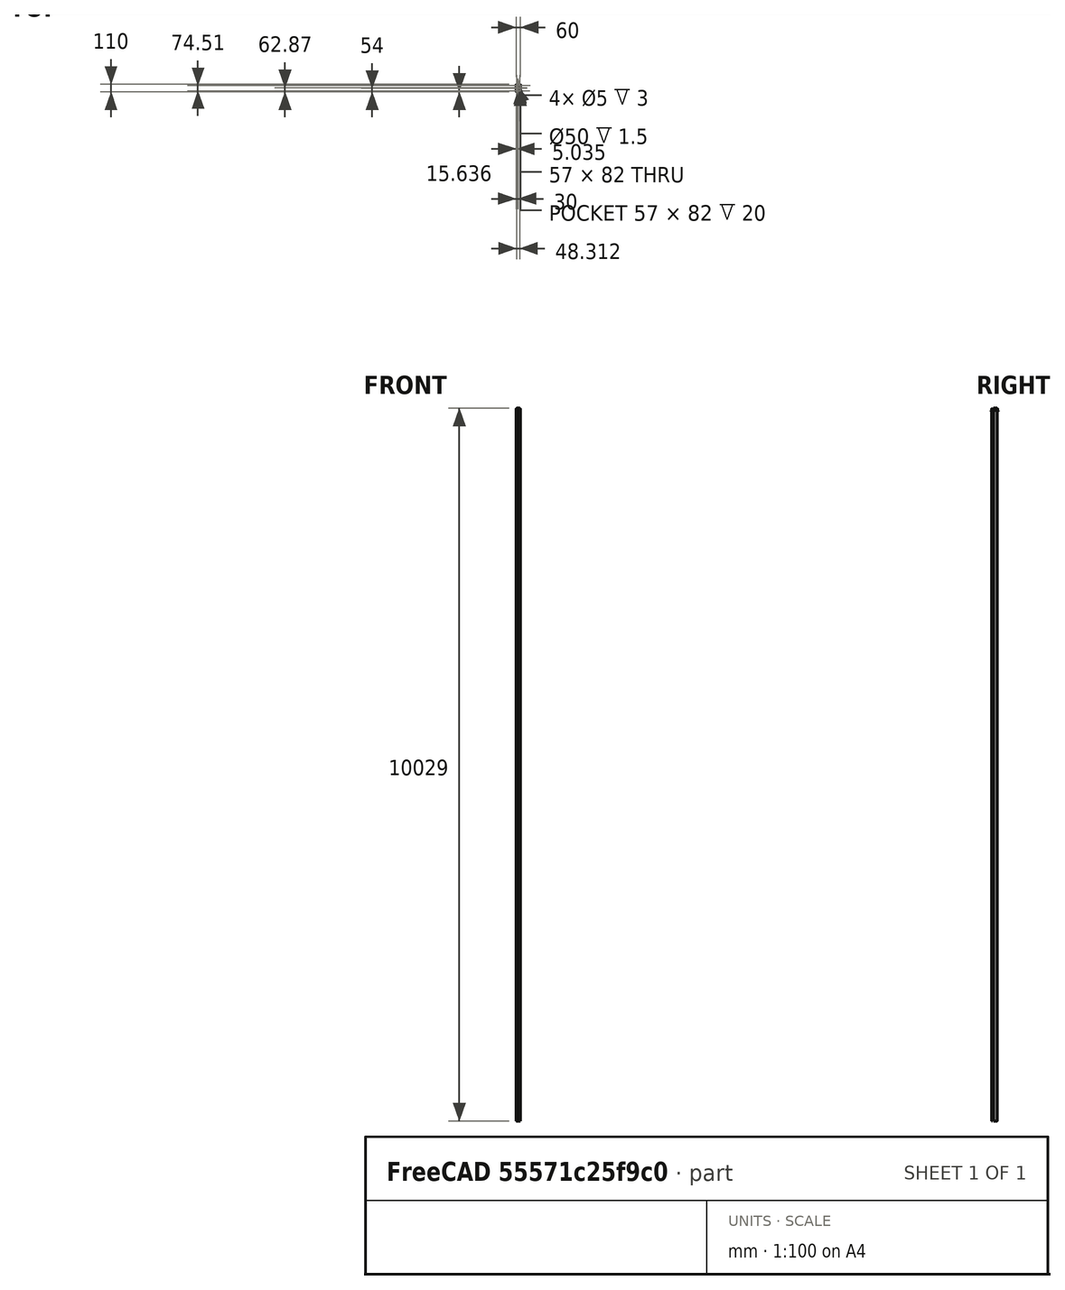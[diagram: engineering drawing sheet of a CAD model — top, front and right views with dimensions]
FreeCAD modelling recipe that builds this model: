
FCSTD DOCUMENT  (FreeCAD 0.16R4740 (Git))
Label: NotifierEnclosurev2
License: CC-BY 3.0
LicenseURL: http://creativecommons.org/licenses/by/3.0/
objects: Sketcher::SketchObject×11, Part::Box×6, Part::FeaturePython×6, PartDesign::Pad×5, Part::MultiFuse×5, Part::Cut×5, PartDesign::Pocket×4, App::DocumentObjectGroup×2, Part::Thickness×2, Part::Part2DObjectPython×2, PartDesign::Fillet×2, Part::Offset×2, Part::Sweep×2, Part::Cylinder×1, Part::Fillet×1
note: 63 computed .brp shape members not serialized (recipe doc carries the construction recipe); baked Part::Feature solids carry a one-line shape summary decoded from their .brp

FEATURE [Part::Box] Box  label="Cube"
  Height = 20
  Length = 57
  Width = 82
FEATURE [Part::Box] Box001  label="Base"
  Height = 1.6
  Length = 54
  Placement = pos=(0,0,3) rot=(0,0,1;0rad)
  Width = 80
FEATURE [Part::Box] Box002  label="EthernetJack"
  Height = 13.6
  Length = 16
  Placement = pos=(11.2,-4.6,4.6) rot=(0,0,1;0rad)
  Width = 21
FEATURE [Part::Box] Box003  label="PowerJack"
  Height = 11
  Length = 9
  Placement = pos=(43.4,-4.5,4.6) rot=(0,0,1;0rad)
  Width = 14.5
FEATURE [Sketcher::SketchObject] Sketch
  ExternalGeometry = -> [Box001]
  Placement = pos=(0,0,4.6) rot=(0,0,1;0rad)
  Support = -> Box001 [Face6]
  sketch-geometry (6):
    g0: Circle CenterX=2.2 CenterY=77.12 CenterZ=0 NormalX=0 NormalY=0 NormalZ=1 Radius=1.5
    g1: Circle CenterX=50.25 CenterY=76.75 CenterZ=0 NormalX=0 NormalY=0 NormalZ=1 Radius=1.5
    g2: Circle CenterX=2 CenterY=2.7 CenterZ=0 NormalX=0 NormalY=0 NormalZ=1 Radius=1.5
    g3: Circle CenterX=39.8 CenterY=2.7 CenterZ=0 NormalX=0 NormalY=0 NormalZ=1 Radius=1.5
    g4: LineSegment [constr] StartX=0.5 StartY=1.2 StartZ=0 EndX=0.5 EndY=5.19188 EndZ=0
    g5: LineSegment [constr] StartX=0.5 StartY=1.2 StartZ=0 EndX=4.53205 EndY=1.2 EndZ=0
  constraints (17):
    c: Radius(g2) = 1.5
    c: Vertical(g4)
    c: Tangent(g4,g2)
    c: Horizontal(g5)
    c: Tangent(g5,g2)
    c: Coincident(g4,g5)
    c: DistanceX(g-1,g4) = 0.5
    c: DistanceY(g-1,g5) = 1.2
    c: Equal(g3,g2)
    c: DistanceY(g-1,g3) = 2.7
    c: DistanceX(g3,g-3) = 14.2
    c: Equal(g0,g1)
    c: Equal(g1,g2)
    c: DistanceY(g0,g-4) = 2.88
    c: DistanceX(g0,g-4) = -2.2
    c: DistanceX(g1,g-4) = 3.75
    c: DistanceY(g1,g-4) = 3.25
FEATURE [PartDesign::Pocket] Pocket  label="Holes"
  Length = 5
  Placement = pos=(0,0,3) rot=(0,0,1;0rad)
  Sketch = -> Sketch
  Type = 1
FEATURE [App::DocumentObjectGroup] Group  label="iBoard"
  Group = -> [Box001,Box002,Box003,Pocket]
FEATURE [Part::Thickness] Thickness
  Faces = -> Box [Face6]
  Intersection = false
  Join = 0
  Mode = 0
  Placement = pos=(-1.5,0,0) rot=(0,0,1;0rad)
  SelfIntersection = false
  Value = 1.5
FEATURE [Sketcher::SketchObject] Sketch001
  ExternalGeometry = -> [Thickness]
  Placement = pos=(-1.5,0,20) rot=(0,0,1;0rad)
  Support = -> Thickness [Face6]
  sketch-geometry (8):
    g0: LineSegment StartX=-1.5 StartY=0 StartZ=0 EndX=-1.5 EndY=82 EndZ=0
    g1: LineSegment StartX=0 StartY=83.5 StartZ=0 EndX=57 EndY=83.5 EndZ=0
    g2: LineSegment StartX=58.5 StartY=0 StartZ=0 EndX=58.5 EndY=82 EndZ=0
    g3: LineSegment StartX=0 StartY=-1.5 StartZ=0 EndX=57 EndY=-1.5 EndZ=0
    g4: ArcOfCircle CenterX=0 CenterY=0 CenterZ=0 NormalX=0 NormalY=0 NormalZ=1 Radius=1.5 StartAngle=3.14159 EndAngle=4.71239
    g5: ArcOfCircle CenterX=0 CenterY=82 CenterZ=0 NormalX=0 NormalY=0 NormalZ=1 Radius=1.5 StartAngle=1.5708 EndAngle=3.14159
    g6: ArcOfCircle CenterX=57 CenterY=82 CenterZ=0 NormalX=0 NormalY=0 NormalZ=1 Radius=1.5 StartAngle=0 EndAngle=1.5708
    g7: ArcOfCircle CenterX=57 CenterY=0 CenterZ=0 NormalX=0 NormalY=0 NormalZ=1 Radius=1.5 StartAngle=4.71239 EndAngle=6.28319
  constraints (24):
    c: Vertical(g0)
    c: Horizontal(g1)
    c: Vertical(g2)
    c: Horizontal(g3)
    c: Coincident(g0,g-10)
    c: Coincident(g0,g-4)
    c: Coincident(g-10,g3)
    c: Coincident(g3,g-9)
    c: Coincident(g2,g-8)
    c: Coincident(g2,g-7)
    c: Coincident(g1,g-6)
    c: Coincident(g1,g-5)
    c: Coincident(g4,g-1)
    c: Coincident(g4,g3)
    c: Coincident(g4,g0)
    c: Coincident(g5,g-3)
    c: Coincident(g5,g0)
    c: Coincident(g5,g1)
    c: Coincident(g6,g-6)
    c: Coincident(g6,g1)
    c: Coincident(g6,g2)
    c: Coincident(g7,g-8)
    c: Coincident(g7,g2)
    c: Coincident(g7,g3)
FEATURE [Part::Part2DObjectPython] Clone2D  label="Clone of Sketch001 (2D)"  # Draft 2D object (typed FeaturePython)
  Objects = -> [Sketch001]
  Placement = pos=(-1.5,0,20) rot=(0,0,1;0rad)
  Scale = (1,1,1)
FEATURE [PartDesign::Pad] Pad
  Length = 1.5
  Length2 = 100
  Placement = pos=(-1.5,0,20) rot=(0,0,1;0rad)
  Sketch = -> Clone2D
  Type = 0
FEATURE [PartDesign::Fillet] Fillet
  Base = -> Pad [Edge22,Edge24,Edge19,Edge13,Edge7,Edge4,Edge16,Edge10]
  Placement = pos=(-1.5,0,20) rot=(0,0,1;0rad)
  Radius = 0.5
FEATURE [Sketcher::SketchObject] Sketch002
  ExternalGeometry = -> [Fillet]
  Placement = pos=(-1.5,0,21.5) rot=(0,0,1;0rad)
  Support = -> Fillet [Face8]
  sketch-geometry (2):
    g0: Circle CenterX=28.5 CenterY=49.8696 CenterZ=0 NormalX=0 NormalY=0 NormalZ=1 Radius=25
    g1: LineSegment [constr] StartX=28.5 StartY=49.8696 StartZ=0 EndX=28.5 EndY=88.1673 EndZ=0
  constraints (4):
    c: Radius(g0) = 25
    c: Coincident(g1,g0)
    c: Vertical(g1)
    c: Symmetric(g-5,g-3,g1)
FEATURE [PartDesign::Pocket] Pocket001
  Length = 5
  Placement = pos=(-1.5,0,20) rot=(0,0,1;0rad)
  Sketch = -> Sketch002
  Type = 1
FEATURE [Sketcher::SketchObject] Sketch003
  Placement = pos=(-1.5,0,0) rot=(0,0,1;0rad)
  Support = -> Thickness [Face5]
  sketch-geometry (4):
    g0: Circle CenterX=3.53528 CenterY=2.63614 CenterZ=0 NormalX=0 NormalY=0 NormalZ=1 Radius=2.5
    g1: Circle CenterX=41.3722 CenterY=2.74074 CenterZ=0 NormalX=0 NormalY=0 NormalZ=1 Radius=2.5
    g2: Circle CenterX=3.78181 CenterY=77.146 CenterZ=0 NormalX=0 NormalY=0 NormalZ=1 Radius=2.5
    g3: Circle CenterX=51.8469 CenterY=76.7239 CenterZ=0 NormalX=0 NormalY=0 NormalZ=1 Radius=2.5
  constraints (4):
    c: Radius(g0) = 2.5
    c: Equal(g0,g1)
    c: Equal(g1,g2)
    c: Equal(g2,g3)
FEATURE [PartDesign::Pad] Pad001
  Length = 3
  Length2 = 100
  Placement = pos=(-1.5,0,0) rot=(0,0,1;0rad)
  Sketch = -> Sketch003
  Type = 0
FEATURE [Sketcher::SketchObject] Sketch004
  ExternalGeometry = -> [Pad001]
  Placement = pos=(-1.5,0,3) rot=(0,0,1;0rad)
  Support = -> Pad001 [Face30]
  sketch-geometry (4):
    g0: Circle CenterX=3.78181 CenterY=77.146 CenterZ=0 NormalX=0 NormalY=0 NormalZ=1 Radius=1.4
    g1: Circle CenterX=51.8469 CenterY=76.7239 CenterZ=0 NormalX=0 NormalY=0 NormalZ=1 Radius=1.4
    g2: Circle CenterX=3.53528 CenterY=2.63614 CenterZ=0 NormalX=0 NormalY=0 NormalZ=1 Radius=1.4
    g3: Circle CenterX=41.3722 CenterY=2.74074 CenterZ=0 NormalX=0 NormalY=0 NormalZ=1 Radius=1.4
  constraints (8):
    c: Coincident(g0,g-3)
    c: Coincident(g1,g-4)
    c: Coincident(g2,g-5)
    c: Coincident(g3,g-6)
    c: Radius(g1) = 1.4
    c: Equal(g1,g0)
    c: Equal(g0,g2)
    c: Equal(g2,g3)
FEATURE [PartDesign::Pocket] Pocket002
  Length = 3
  Placement = pos=(-1.5,0,0) rot=(0,0,1;0rad)
  Sketch = -> Sketch004
  Type = 0
FEATURE [Sketcher::SketchObject] Sketch005
  ExternalGeometry = -> [Pocket001]
  Placement = pos=(-1.5,0,20) rot=(1,0,0;3.14159rad)
  Support = -> Pocket001 [Face4]
  sketch-geometry (8):
    g0: LineSegment StartX=0.2 StartY=-0.2 StartZ=0 EndX=56.8 EndY=-0.2 EndZ=0
    g1: LineSegment StartX=56.8 StartY=-0.2 StartZ=0 EndX=56.8 EndY=-81.8 EndZ=0
    g2: LineSegment StartX=56.8 StartY=-81.8 StartZ=0 EndX=0.2 EndY=-81.8 EndZ=0
    g3: LineSegment StartX=0.2 StartY=-81.8 StartZ=0 EndX=0.2 EndY=-0.2 EndZ=0
    g4: LineSegment StartX=1.5 StartY=-1.5 StartZ=0 EndX=55.5 EndY=-1.5 EndZ=0
    g5: LineSegment StartX=55.5 StartY=-1.5 StartZ=0 EndX=55.5 EndY=-80.5 EndZ=0
    g6: LineSegment StartX=55.5 StartY=-80.5 StartZ=0 EndX=1.5 EndY=-80.5 EndZ=0
    g7: LineSegment StartX=1.5 StartY=-80.5 StartZ=0 EndX=1.5 EndY=-1.5 EndZ=0
  constraints (12):
    c: DistanceX(g-1,g3) = 0.2
    c: DistanceY(g-1,g0) = -0.2
    c: Coincident(g0,g3)
    c: DistanceY(g0,g-3) = 0.2
    c: DistanceX(g1,g-3) = 0.2
    c: Coincident(g1,g0)
    c: DistanceX(g1,g-6) = 0.2
    c: DistanceY(g2,g-6) = -0.2
    c: Coincident(g2,g1)
    c: DistanceX(g3,g-5) = -0.2
    c: DistanceY(g2,g-5) = -0.2
    c: Coincident(g2,g3)
FEATURE [PartDesign::Pad] Pad002
  Length = 2
  Length2 = 100
  Placement = pos=(-1.5,0,20) rot=(0,0,1;0rad)
  Sketch = -> Sketch005
  Type = 0
FEATURE [App::DocumentObjectGroup] Group001  label="Lid"
  Group = -> [Pad,Fillet,Pocket001,Pad002]
FEATURE [Part::Box] Box004  label="Tab1"
  Height = 10
  Length = 8
  Placement = pos=(0,0.2,8) rot=(0,0,1;0rad)
  Width = 1.5
FEATURE [Part::FeaturePython] Clone  label="Clone of Tab1"  # Draft clone (typed FeaturePython)
  Objects = -> [Box004]
  Placement = pos=(32,0.2,8) rot=(0,0,1;0rad)
  Scale = (1,1,1)
FEATURE [Part::FeaturePython] Clone001  label="Clone of Tab002"  # Draft clone (typed FeaturePython)
  Objects = -> [Box004]
  Placement = pos=(0,80.3,8) rot=(0,0,1;0rad)
  Scale = (1,1,1)
FEATURE [Part::FeaturePython] Clone002  label="Clone of Tab003"  # Draft clone (typed FeaturePython)
  Objects = -> [Box004]
  Placement = pos=(46,80.3,8) rot=(0,0,1;0rad)
  Scale = (1,1,1)
FEATURE [Part::Cylinder] Cylinder
  Angle = 360
  Height = 10
  Placement = pos=(4,6,14) rot=(1,0,0;1.5708rad)
  Radius = 1.4
FEATURE [Part::MultiFuse] Fusion  label="LidFusion"
  Shapes = -> [Pad002,Box004,Clone,Clone001,Clone002]
FEATURE [Part::FeaturePython] Clone003  label="Clone of Cylinder"  # Draft clone (typed FeaturePython)
  Objects = -> [Cylinder]
  Placement = pos=(36,6,14) rot=(1,0,0;1.5708rad)
  Scale = (1,1,1)
FEATURE [Part::FeaturePython] Clone004  label="Clone of Cylinder001"  # Draft clone (typed FeaturePython)
  Objects = -> [Cylinder]
  Placement = pos=(4,86,14) rot=(1,0,0;1.5708rad)
  Scale = (1,1,1)
FEATURE [Part::FeaturePython] Clone005  label="Clone of Cylinder002"  # Draft clone (typed FeaturePython)
  Objects = -> [Cylinder]
  Placement = pos=(50,86,14) rot=(1,0,0;1.5708rad)
  Scale = (1,1,1)
FEATURE [Part::MultiFuse] Fusion001
  Shapes = -> [Clone005,Clone004,Clone003,Cylinder]
FEATURE [Part::Cut] Cut
  Base = -> Fusion
  Tool = -> Fusion001
FEATURE [Part::Cut] Cut001
  Base = -> Pocket002
  Tool = -> Fusion001
FEATURE [Part::Offset] Offset
  Fill = false
  Intersection = false
  Join = 2
  Mode = 0
  SelfIntersection = false
  Source = -> Box002
  Value = 1
FEATURE [Part::Offset] Offset001
  Fill = false
  Intersection = false
  Join = 2
  Mode = 0
  SelfIntersection = false
  Source = -> Box003
  Value = 1
FEATURE [Part::MultiFuse] Fusion002
  Shapes = -> [Offset,Offset001]
FEATURE [Part::Cut] Cut002
  Base = -> Cut001
  Tool = -> Fusion002
FEATURE [Part::Cut] Cut003  label="Lid001"
  Base = -> Cut
  Tool = -> Offset
FEATURE [Sketcher::SketchObject] Sketch006
  ExternalGeometry = -> [Cut003]
  Placement = pos=(0,0,21.5) rot=(0,0,1;0rad)
  Support = -> Cut003 [Face60]
  sketch-geometry (1):
    g0: Circle CenterX=27 CenterY=49.8696 CenterZ=0 NormalX=0 NormalY=0 NormalZ=1 Radius=24.5
  constraints (2):
    c: Coincident(g0,g-3)
    c: Radius(g0) = 24.5
FEATURE [Part::Part2DObjectPython] Clone2D001  label="Clone of Sketch006 (2D)"  # Draft 2D object (typed FeaturePython)
  Objects = -> [Sketch006]
  Placement = pos=(0,0,20.5) rot=(0,0,1;0rad)
  Scale = (1,1,1)
FEATURE [PartDesign::Pad] Pad003
  Length = 10
  Length2 = 100
  Placement = pos=(0,0,20.5) rot=(0,0,1;0rad)
  Sketch = -> Clone2D001
  Type = 0
FEATURE [PartDesign::Fillet] Fillet001
  Base = -> Pad003 [Edge3]
  Placement = pos=(0,0,20.5) rot=(0,0,1;0rad)
  Radius = 5
FEATURE [Sketcher::SketchObject] Sketch007
  ExternalGeometry = -> [Fillet001]
  Placement = pos=(0,0,20.5) rot=(1,0,0;3.14159rad)
  Support = -> Fillet001 [Face3]
  sketch-geometry (1):
    g0: Circle CenterX=27 CenterY=-49.8696 CenterZ=0 NormalX=0 NormalY=0 NormalZ=1 Radius=26.5
  constraints (2):
    c: Coincident(g0,g-3)
    c: Radius(g0) = 26.5
FEATURE [PartDesign::Pad] Pad004
  Length = 1.5
  Length2 = 100
  Placement = pos=(0,0,20.5) rot=(0,0,1;0rad)
  Sketch = -> Sketch007
  Type = 0
FEATURE [Part::Thickness] Thickness001
  Faces = -> Pad004 [Face3]
  Intersection = false
  Join = 0
  Mode = 0
  SelfIntersection = false
  Value = -1.5
FEATURE [Part::Box] Box005  label="Cube001"
  Height = 1.5
  Length = 58
  Placement = pos=(-2,-13,-1.5) rot=(0,0,1;0rad)
  Width = 110
FEATURE [Part::Fillet] Fillet002
  Base = -> Box005
  Edges = 4 edges r=5: [Edge1,Edge3,Edge5,Edge7]
FEATURE [Sketcher::SketchObject] Sketch008
  ExternalGeometry = -> [Fillet002]
  Support = -> Fillet002 [Face2]
  sketch-geometry (4):
    g0: Circle CenterX=3 CenterY=92 CenterZ=0 NormalX=0 NormalY=0 NormalZ=1 Radius=1.5
    g1: Circle CenterX=51 CenterY=92 CenterZ=0 NormalX=0 NormalY=0 NormalZ=1 Radius=1.5
    g2: Circle CenterX=3 CenterY=-8 CenterZ=0 NormalX=0 NormalY=0 NormalZ=1 Radius=1.5
    g3: Circle CenterX=51 CenterY=-8 CenterZ=0 NormalX=0 NormalY=0 NormalZ=1 Radius=1.5
  constraints (8):
    c: Radius(g0) = 1.5
    c: Equal(g0,g1)
    c: Equal(g1,g3)
    c: Equal(g3,g2)
    c: Coincident(g2,g-6)
    c: Coincident(g3,g-5)
    c: Coincident(g0,g-3)
    c: Coincident(g1,g-4)
FEATURE [PartDesign::Pocket] Pocket003
  Length = 5
  Sketch = -> Sketch008
  Type = 0
FEATURE [Part::MultiFuse] Fusion003
  Shapes = -> [Cut002,Pocket003]
FEATURE [Part::Cut] Cut004
  Base = -> Fusion003
FEATURE [Sketcher::SketchObject] Sketch009
  ExternalGeometry = -> [Cut003]
  Placement = pos=(0,0.2,0) rot=(1,0,0;1.5708rad)
  Support = -> Cut003 [Face22]
  sketch-geometry (4):
    g0: LineSegment StartX=-1.3 StartY=18.75 StartZ=0 EndX=-1.94952 EndY=18.375 EndZ=0
    g1: LineSegment StartX=-1.94952 StartY=18.375 StartZ=0 EndX=-1.3 EndY=18 EndZ=0
    g2: LineSegment StartX=-1.3 StartY=18 StartZ=0 EndX=-1.3 EndY=18.75 EndZ=0
    g3: Circle [constr] CenterX=-1.51651 CenterY=18.375 CenterZ=0 NormalX=0 NormalY=0 NormalZ=1 Radius=0.433013
  constraints (11):
    c: Coincident(g0,g1)
    c: Coincident(g1,g2)
    c: Coincident(g2,g0)
    c: Equal(g0,g1)
    c: Equal(g0,g2)
    c: PointOnObject(g0,g3)
    c: PointOnObject(g1,g3)
    c: PointOnObject(g2,g3)
    c: Vertical(g2)
    c: DistanceY(g1,g0) = 0.75
    c: Coincident(g1,g-3)
FEATURE [Part::Sweep] Sweep
  Frenet = false
  Sections = -> [Sketch009]
  Solid = true
  Spine = -> Cut003 [Edge56]
  Transition = 1
FEATURE [Sketcher::SketchObject] Sketch010
  ExternalGeometry = -> [Cut003]
  Placement = pos=(0,0.2,0) rot=(1,0,0;1.5708rad)
  Support = -> Cut003 [Face22]
  sketch-geometry (4):
    g0: LineSegment StartX=55.3 StartY=18.75 StartZ=0 EndX=55.3 EndY=18 EndZ=0
    g1: LineSegment StartX=55.3 StartY=18 StartZ=0 EndX=55.9495 EndY=18.375 EndZ=0
    g2: LineSegment StartX=55.9495 StartY=18.375 StartZ=0 EndX=55.3 EndY=18.75 EndZ=0
    g3: Circle [constr] CenterX=55.5165 CenterY=18.375 CenterZ=0 NormalX=0 NormalY=0 NormalZ=1 Radius=0.433013
  constraints (11):
    c: Coincident(g0,g1)
    c: Coincident(g1,g2)
    c: Coincident(g2,g0)
    c: Equal(g0,g1)
    c: Equal(g0,g2)
    c: PointOnObject(g0,g3)
    c: PointOnObject(g1,g3)
    c: PointOnObject(g2,g3)
    c: Vertical(g0)
    c: DistanceY(g0,g0) = -0.75
    c: Coincident(g-3,g0)
FEATURE [Part::Sweep] Sweep001
  Frenet = false
  Sections = -> [Sketch010]
  Solid = true
  Spine = -> Cut003 [Edge32]
  Transition = 1
FEATURE [Part::MultiFuse] Fusion004
  Shapes = -> [Cut003,Sweep001,Sweep]
